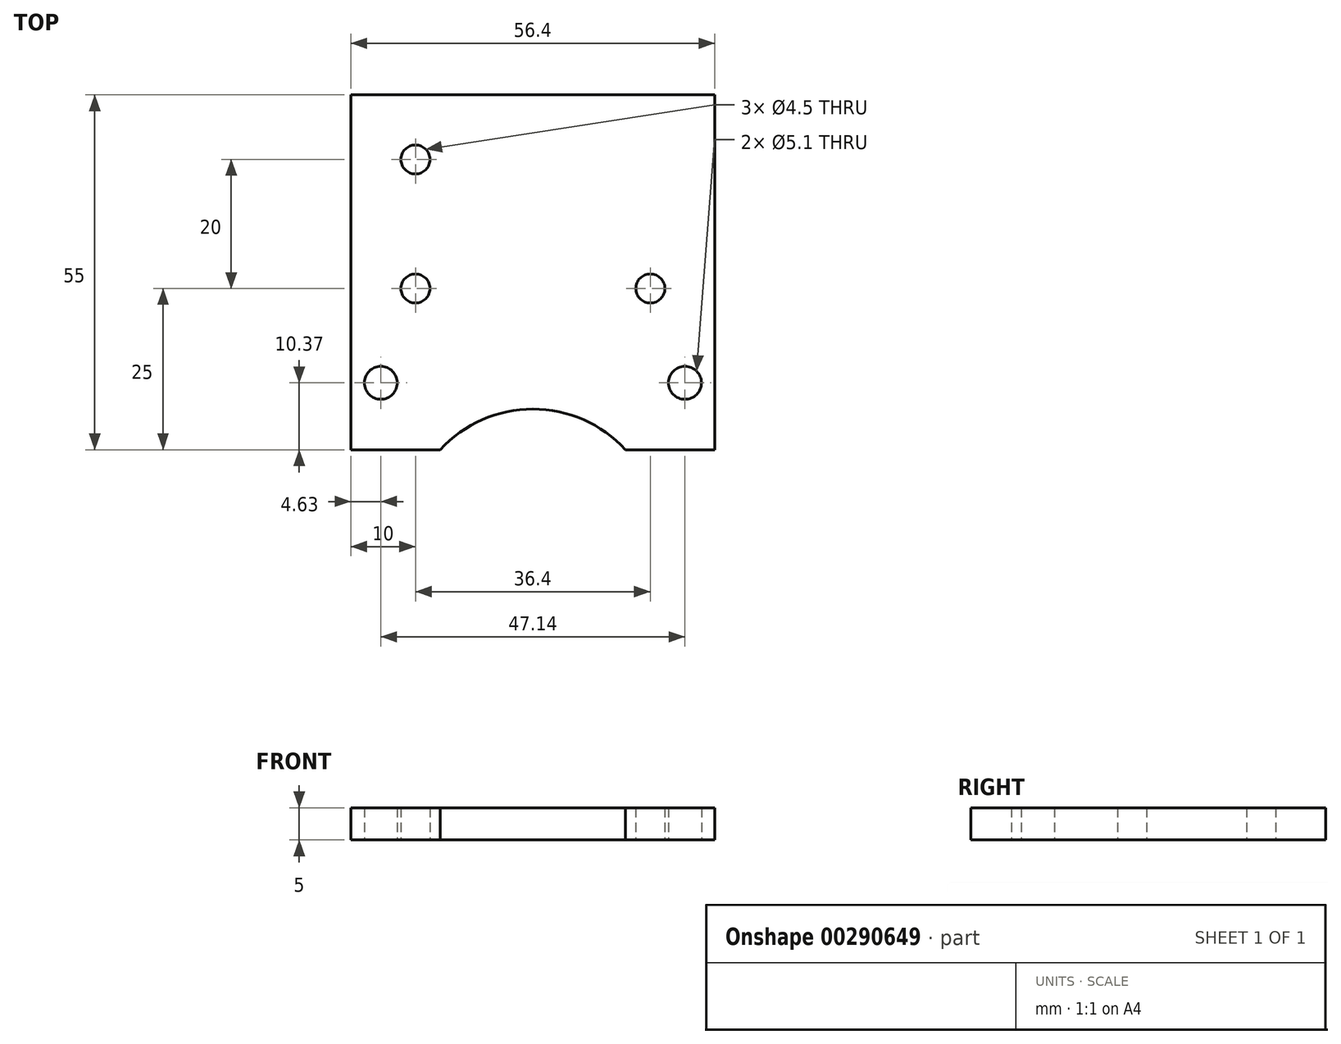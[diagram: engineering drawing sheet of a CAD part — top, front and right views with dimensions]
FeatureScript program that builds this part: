
annotation { "Feature Type Name" : "Feature", "Feature Type Description" : "" }
export const myFeature = defineFeature(function(context is Context, id is Id, definition is map)
    precondition{}
    {
        {
            var Q0;
            Q0=qCreatedBy(makeId("Top.planeOp"),FACE);
            var sketch = newSketch(context, id + "F0", { "sketchPlane" : qUnion([Q0])});
            skLineSegment(sketch, "E0.rect.bottom", {"start": v(-28.2, 28.2) * mm, "end": v(28.2, 28.2) * mm});
            skLineSegment(sketch, "E0.rect.left", {"start": v(-28.2, 28.2) * mm, "end": v(-28.2, 13.2) * mm});
            skLineSegment(sketch, "E0.rect.right", {"start": v(28.2, 28.2) * mm, "end": v(28.2, 13.2) * mm});
            skPoint(sketch, "E0.rect.middle", {"position": v(0, 0) * mm});
            skArc(sketch, "E1", {"start": v(14.35, 13.2) * mm, "mid": v(0, 19.5) * mm, "end": v(-14.35, 13.2) * mm});
            skCircle(sketch, "E2", {"center": v(-23.57, 23.57) * mm, "radius": 2.55 * mm});
            skCircle(sketch, "E3", {"center": v(23.57, 23.57) * mm, "radius": 2.55 * mm});
            skLineSegment(sketch, "E4.rect.bottom", {"start": v(-23.57, 23.57) * mm, "end": v(23.57, 23.57) * mm, "construction": true});
            skLineSegment(sketch, "E4.rect.left", {"start": v(-23.57, 23.57) * mm, "end": v(-23.57, 13.2) * mm, "construction": true});
            skLineSegment(sketch, "E4.rect.right", {"start": v(23.57, 23.57) * mm, "end": v(23.57, 13.2) * mm, "construction": true});
            skLineSegment(sketch, "E5", {"start": v(-28.2, 13.2) * mm, "end": v(-14.35, 13.2) * mm});
            skLineSegment(sketch, "E6.trimOffspring", {"start": v(14.35, 13.2) * mm, "end": v(28.2, 13.2) * mm});
            skLineSegment(sketch, "E7.top", {"start": v(-28.2, 68.2) * mm, "end": v(28.2, 68.2) * mm});
            skLineSegment(sketch, "E7.left", {"start": v(-28.2, 28.2) * mm, "end": v(-28.2, 68.2) * mm});
            skLineSegment(sketch, "E7.right", {"start": v(28.2, 28.2) * mm, "end": v(28.2, 68.2) * mm});
            skLineSegment(sketch, "E8", {"start": v(-28.2, 38.2) * mm, "end": v(28.2, 38.2) * mm, "construction": true});
            skLineSegment(sketch, "E9", {"start": v(-18.2, 28.2) * mm, "end": v(-18.2, 68.2) * mm, "construction": true});
            skCircle(sketch, "E10", {"center": v(-18.2, 38.2) * mm, "radius": 2.25 * mm});
            skCircle(sketch, "E11", {"center": v(-18.2, 58.2) * mm, "radius": 2.25 * mm});
            skCircle(sketch, "E12", {"center": v(18.2, 38.2) * mm, "radius": 2.25 * mm});
            skSolve(sketch);
        }
        {
            var Q0;
            Q0=makeQuery(id+"F0.imprint","IMPRINT",FACE,{"disambiguationData":[TD([[makeQuery(id+"F0.imprint","IMPRINT",EDGE,{"derivedFrom":sQuery(id+"F0.wireOp",EDGE,"E0.rect.bottom")}),1.0]])]});
            var Q1;
            Q1=makeQuery(id+"F0.imprint","IMPRINT",FACE,{"disambiguationData":[TD([[makeQuery(id+"F0.imprint","IMPRINT",EDGE,{"derivedFrom":sQuery(id+"F0.wireOp",EDGE,"E0.rect.left")}),1.0]])]});
            extrude(context, id + "F1", {"entities" : qUnion([Q0, Q1]), "depth" : 5 * mm});
        }
    });
